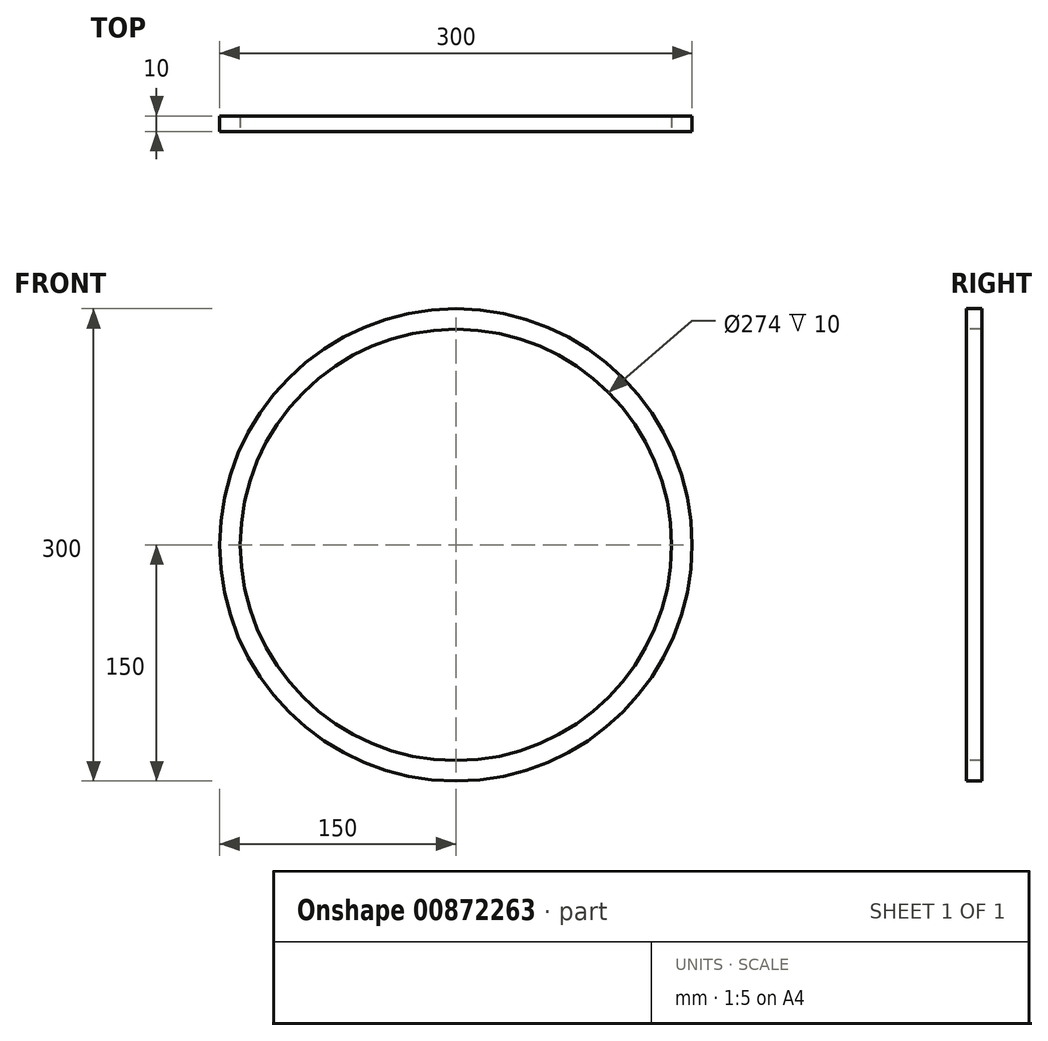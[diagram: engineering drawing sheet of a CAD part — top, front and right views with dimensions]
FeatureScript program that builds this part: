
annotation { "Feature Type Name" : "Feature", "Feature Type Description" : "" }
export const myFeature = defineFeature(function(context is Context, id is Id, definition is map)
    precondition{}
    {
        {
            var Q0;
            Q0=qCreatedBy(makeId("Front.planeOp"),FACE);
            var sketch = newSketch(context, id + "F0", { "sketchPlane" : qUnion([Q0])});
            skCircle(sketch, "E0", {"center": v(0, 0) * mm, "radius": 150 * mm});
            skSolve(sketch);
        }
        {
            var Q0;
            Q0=makeQuery(id+"F0.imprint","IMPRINT",FACE,{"disambiguationData":[TD([[makeQuery(id+"F0.imprint","IMPRINT",EDGE,{"derivedFrom":sQuery(id+"F0.wireOp",EDGE,"E0")}),1.0]])]});
            extrude(context, id + "F1", {"entities" : qUnion([Q0]), "endBound" : BoundingType.SYMMETRIC, "depth" : 10 * mm, "offsetDistance" : 25 * mm});
        }
        {
            var Q0;
            Q0=makeQuery(id+"F1.opExtrude","CAP_FACE",FACE,{"disambiguationData":[OSD([sQuery(id+"F0.wireOp",EDGE,"E0")])],"isStart":false});
            var sketch = newSketch(context, id + "F2", { "sketchPlane" : qUnion([Q0])});
            skCircle(sketch, "E1", {"center": v(0, 0) * mm, "radius": 137 * mm});
            skSolve(sketch);
        }
        {
            var Q0;
            Q0=makeQuery(id+"F2.imprint","IMPRINT",FACE,{"disambiguationData":[TD([[makeQuery(id+"F2.imprint","IMPRINT",EDGE,{"derivedFrom":sQuery(id+"F2.wireOp",EDGE,"E1")}),1.0]])]});
            extrude(context, id + "F3", {"entities" : qUnion([Q0]), "operationType" : NewBodyOperationType.REMOVE, "endBound" : BoundingType.UP_TO_NEXT, "oppositeDirection" : true, "depth" : 25 * mm, "offsetDistance" : 25 * mm});
        }
    });
